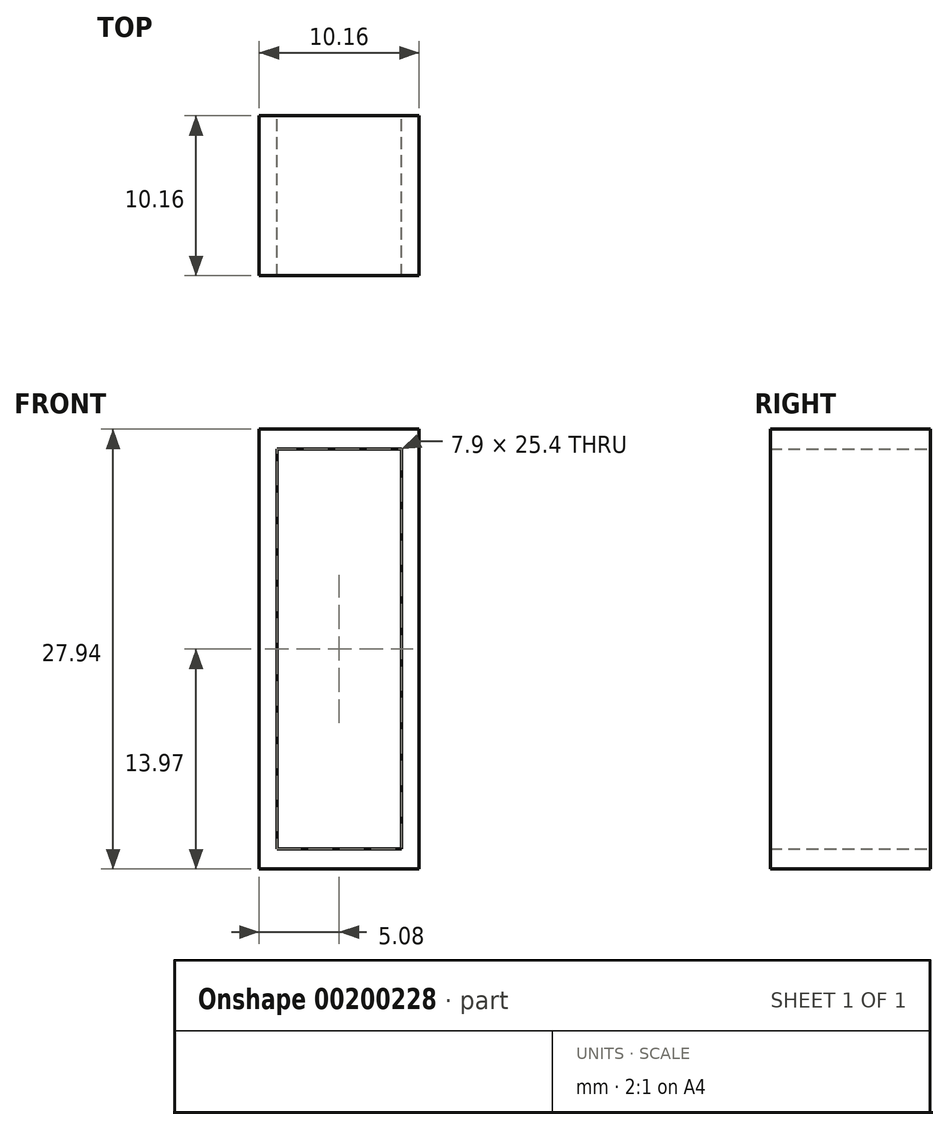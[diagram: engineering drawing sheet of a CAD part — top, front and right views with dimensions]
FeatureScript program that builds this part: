
annotation { "Feature Type Name" : "Feature", "Feature Type Description" : "" }
export const myFeature = defineFeature(function(context is Context, id is Id, definition is map)
    precondition{}
    {
        {
            var Q0;
            Q0=qCreatedBy(makeId("Front.planeOp"),FACE);
            var sketch = newSketch(context, id + "F0", { "sketchPlane" : qUnion([Q0])});
            skLineSegment(sketch, "E0.bottom", {"start": v(-5.08, 13.97) * mm, "end": v(5.08, 13.97) * mm});
            skLineSegment(sketch, "E0.top", {"start": v(-5.08, -13.97) * mm, "end": v(5.08, -13.97) * mm});
            skLineSegment(sketch, "E0.left", {"start": v(-5.08, 13.97) * mm, "end": v(-5.08, -13.97) * mm});
            skLineSegment(sketch, "E0.right", {"start": v(5.08, 13.97) * mm, "end": v(5.08, -13.97) * mm});
            skPoint(sketch, "E0.middle", {"position": v(0, 0) * mm});
            skLineSegment(sketch, "E1.bottom", {"start": v(-3.95, 12.7) * mm, "end": v(3.95, 12.7) * mm});
            skLineSegment(sketch, "E1.top", {"start": v(-3.95, -12.7) * mm, "end": v(3.95, -12.7) * mm});
            skLineSegment(sketch, "E1.left", {"start": v(-3.95, 12.7) * mm, "end": v(-3.95, -12.7) * mm});
            skLineSegment(sketch, "E1.right", {"start": v(3.95, 12.7) * mm, "end": v(3.95, -12.7) * mm});
            skSolve(sketch);
        }
        {
            var Q0;
            Q0 = qSketchRegion(id + "F0", true);
            extrude(context, id + "F1", {"entities" : qUnion([Q0]), "depth" : 10.16 * mm});
        }
    });
